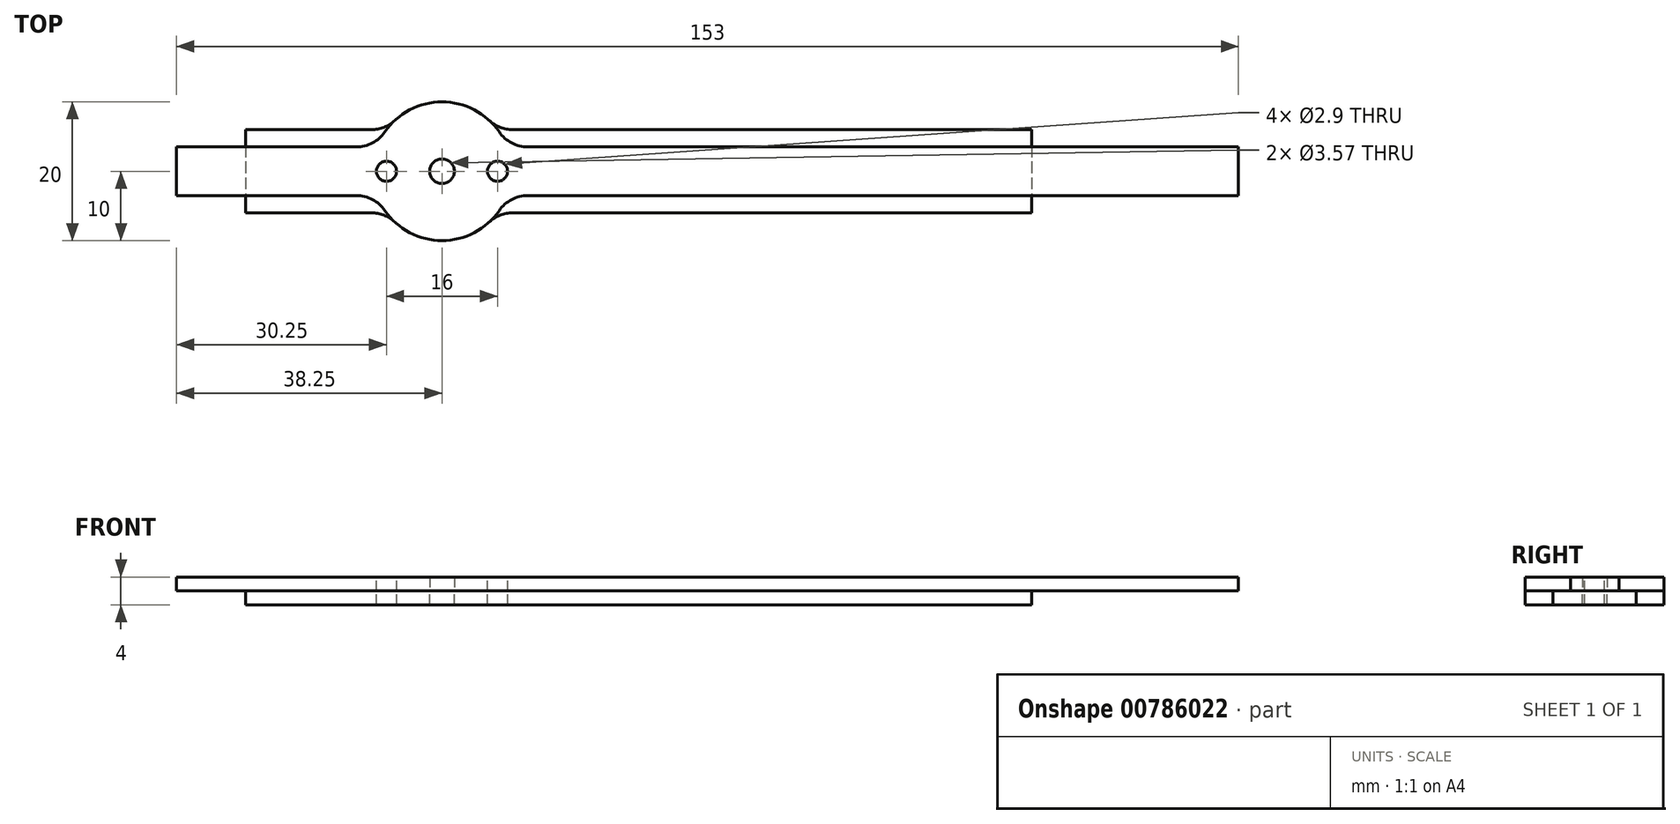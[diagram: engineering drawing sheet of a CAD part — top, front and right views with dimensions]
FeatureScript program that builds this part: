
annotation { "Feature Type Name" : "Feature", "Feature Type Description" : "" }
export const myFeature = defineFeature(function(context is Context, id is Id, definition is map)
    precondition{}
    {
        {
            var Q0;
            Q0=qCreatedBy(makeId("Top.planeOp"),FACE);
            var sketch = newSketch(context, id + "F0", { "sketchPlane" : qUnion([Q0])});
            skCircle(sketch, "E0", {"center": v(0, 0) * mm, "radius": 1.79 * mm});
            skLineSegment(sketch, "E1.bottom", {"start": v(-38.25, 3.5) * mm, "end": v(114.75, 3.5) * mm});
            skLineSegment(sketch, "E1.top", {"start": v(-38.25, -3.5) * mm, "end": v(114.75, -3.5) * mm});
            skLineSegment(sketch, "E1.left", {"start": v(-38.25, 3.5) * mm, "end": v(-38.25, -3.5) * mm});
            skLineSegment(sketch, "E1.right", {"start": v(114.75, 3.5) * mm, "end": v(114.75, -3.5) * mm});
            skCircle(sketch, "E2", {"center": v(0, 0) * mm, "radius": 10 * mm});
            skSolve(sketch);
        }
        {
            var Q0;
            Q0=qSketchRegion(id+"F0",true);
            extrude(context, id + "F1", {"entities" : qUnion([Q0]), "depth" : 2 * mm});
        }
        {
            var Q0;
            Q0=qCreatedBy(makeId("Top.planeOp"),FACE);
            var sketch = newSketch(context, id + "F2", { "sketchPlane" : qUnion([Q0])});
            skCircle(sketch, "E3", {"center": v(0, 0) * mm, "radius": 1.79 * mm});
            skLineSegment(sketch, "E4.bottom", {"start": v(-28.33, 6) * mm, "end": v(85, 6) * mm});
            skLineSegment(sketch, "E4.top", {"start": v(-28.33, -6) * mm, "end": v(85, -6) * mm});
            skLineSegment(sketch, "E4.left", {"start": v(-28.33, 6) * mm, "end": v(-28.33, -6) * mm});
            skLineSegment(sketch, "E4.right", {"start": v(85, 6) * mm, "end": v(85, -6) * mm});
            skCircle(sketch, "E5", {"center": v(0, 0) * mm, "radius": 10 * mm});
            skSolve(sketch);
        }
        {
            var Q0;
            Q0=qSketchRegion(id+"F2",true);
            extrude(context, id + "F3", {"entities" : qUnion([Q0]), "oppositeDirection" : true, "depth" : 2 * mm});
        }
        {
            var Q0;
            Q0=makeQuery(id+"F1.opExtrude","CAP_FACE",FACE,{"disambiguationData":[OSD([sQuery(id+"F0.wireOp",EDGE,"E0"),sQuery(id+"F0.wireOp",EDGE,"E1.bottom"),sQuery(id+"F0.wireOp",EDGE,"E1.top"),sQuery(id+"F0.wireOp",EDGE,"E1.left"),sQuery(id+"F0.wireOp",EDGE,"E1.right"),sQuery(id+"F0.wireOp",EDGE,"E2")])],"isStart":false});
            var sketch = newSketch(context, id + "F4", { "sketchPlane" : qUnion([Q0])});
            skCircle(sketch, "E6", {"center": v(8, 0) * mm, "radius": 1.45 * mm});
            skLineSegment(sketch, "E7", {"start": v(0, 0) * mm, "end": v(16, 0) * mm, "construction": true});
            skLineSegment(sketch, "E8", {"start": v(0, 0) * mm, "end": v(0, 19.04) * mm, "construction": true});
            skCircle(sketch, "E9.MirrorC", {"center": v(-8, 0) * mm, "radius": 1.45 * mm});
            skSolve(sketch);
        }
        {
            var Q0;
            Q0=qSketchRegion(id+"F4",true);
            extrude(context, id + "F5", {"entities" : qUnion([Q0]), "operationType" : NewBodyOperationType.REMOVE, "oppositeDirection" : true, "depth" : 25 * mm, "offsetDistance" : 25 * mm});
        }
        {
            var Q0;
            {var subQ0=sQuery(id+"F0.wireOp",EDGE,"E2");var subQ1=sQuery(id+"F0.wireOp",EDGE,"E1.top");Q0=makeQuery(id+"F1.opExtrude","SWEPT_EDGE",EDGE,{"disambiguationData":[OSD([subQ1,subQ0]),TDD([makeQuery(id+"F0.imprint","INTERSECT",VERTEX,{"disambiguationData":[OD(1.0)],"derivedFrom":[subQ1,subQ0]})])]});}
            var Q1;
            {var subQ0=sQuery(id+"F0.wireOp",EDGE,"E2");var subQ1=sQuery(id+"F0.wireOp",EDGE,"E1.bottom");Q1=makeQuery(id+"F1.opExtrude","SWEPT_EDGE",EDGE,{"disambiguationData":[OSD([subQ1,subQ0]),TDD([makeQuery(id+"F0.imprint","INTERSECT",VERTEX,{"disambiguationData":[OD(1.0)],"derivedFrom":[subQ1,subQ0]})])]});}
            var Q2;
            {var subQ0=sQuery(id+"F0.wireOp",EDGE,"E2");var subQ1=sQuery(id+"F0.wireOp",EDGE,"E1.bottom");Q2=makeQuery(id+"F1.opExtrude","SWEPT_EDGE",EDGE,{"disambiguationData":[OSD([subQ1,subQ0]),TDD([makeQuery(id+"F0.imprint","INTERSECT",VERTEX,{"disambiguationData":[OD(0.0)],"derivedFrom":[subQ1,subQ0]})])]});}
            var Q3;
            {var subQ0=sQuery(id+"F0.wireOp",EDGE,"E2");var subQ1=sQuery(id+"F0.wireOp",EDGE,"E1.top");Q3=makeQuery(id+"F1.opExtrude","SWEPT_EDGE",EDGE,{"disambiguationData":[OSD([subQ1,subQ0]),TDD([makeQuery(id+"F0.imprint","INTERSECT",VERTEX,{"disambiguationData":[OD(0.0)],"derivedFrom":[subQ1,subQ0]})])]});}
            var Q4;
            {var subQ0=sQuery(id+"F2.wireOp",EDGE,"E5");var subQ1=sQuery(id+"F2.wireOp",EDGE,"E4.top");Q4=makeQuery(id+"F3.opExtrude","SWEPT_EDGE",EDGE,{"disambiguationData":[OSD([subQ1,subQ0]),TDD([makeQuery(id+"F2.imprint","INTERSECT",VERTEX,{"disambiguationData":[OD(0.0)],"derivedFrom":[subQ1,subQ0]})])]});}
            var Q5;
            {var subQ0=sQuery(id+"F2.wireOp",EDGE,"E5");var subQ1=sQuery(id+"F2.wireOp",EDGE,"E4.bottom");Q5=makeQuery(id+"F3.opExtrude","SWEPT_EDGE",EDGE,{"disambiguationData":[OSD([subQ1,subQ0]),TDD([makeQuery(id+"F2.imprint","INTERSECT",VERTEX,{"disambiguationData":[OD(1.0)],"derivedFrom":[subQ1,subQ0]})])]});}
            var Q6;
            {var subQ0=sQuery(id+"F2.wireOp",EDGE,"E5");var subQ1=sQuery(id+"F2.wireOp",EDGE,"E4.top");Q6=makeQuery(id+"F3.opExtrude","SWEPT_EDGE",EDGE,{"disambiguationData":[OSD([subQ1,subQ0]),TDD([makeQuery(id+"F2.imprint","INTERSECT",VERTEX,{"disambiguationData":[OD(1.0)],"derivedFrom":[subQ1,subQ0]})])]});}
            var Q7;
            {var subQ0=sQuery(id+"F2.wireOp",EDGE,"E5");var subQ1=sQuery(id+"F2.wireOp",EDGE,"E4.bottom");Q7=makeQuery(id+"F3.opExtrude","SWEPT_EDGE",EDGE,{"disambiguationData":[OSD([subQ1,subQ0]),TDD([makeQuery(id+"F2.imprint","INTERSECT",VERTEX,{"disambiguationData":[OD(0.0)],"derivedFrom":[subQ1,subQ0]})])]});}
            fillet(context, id + "F6", {"entities" : qUnion([Q0, Q1, Q2, Q3, Q4, Q5, Q6, Q7]), "radius" : 5 * mm, "tangentPropagation" : true, "allowEdgeOverflow" : false});
        }
    });
